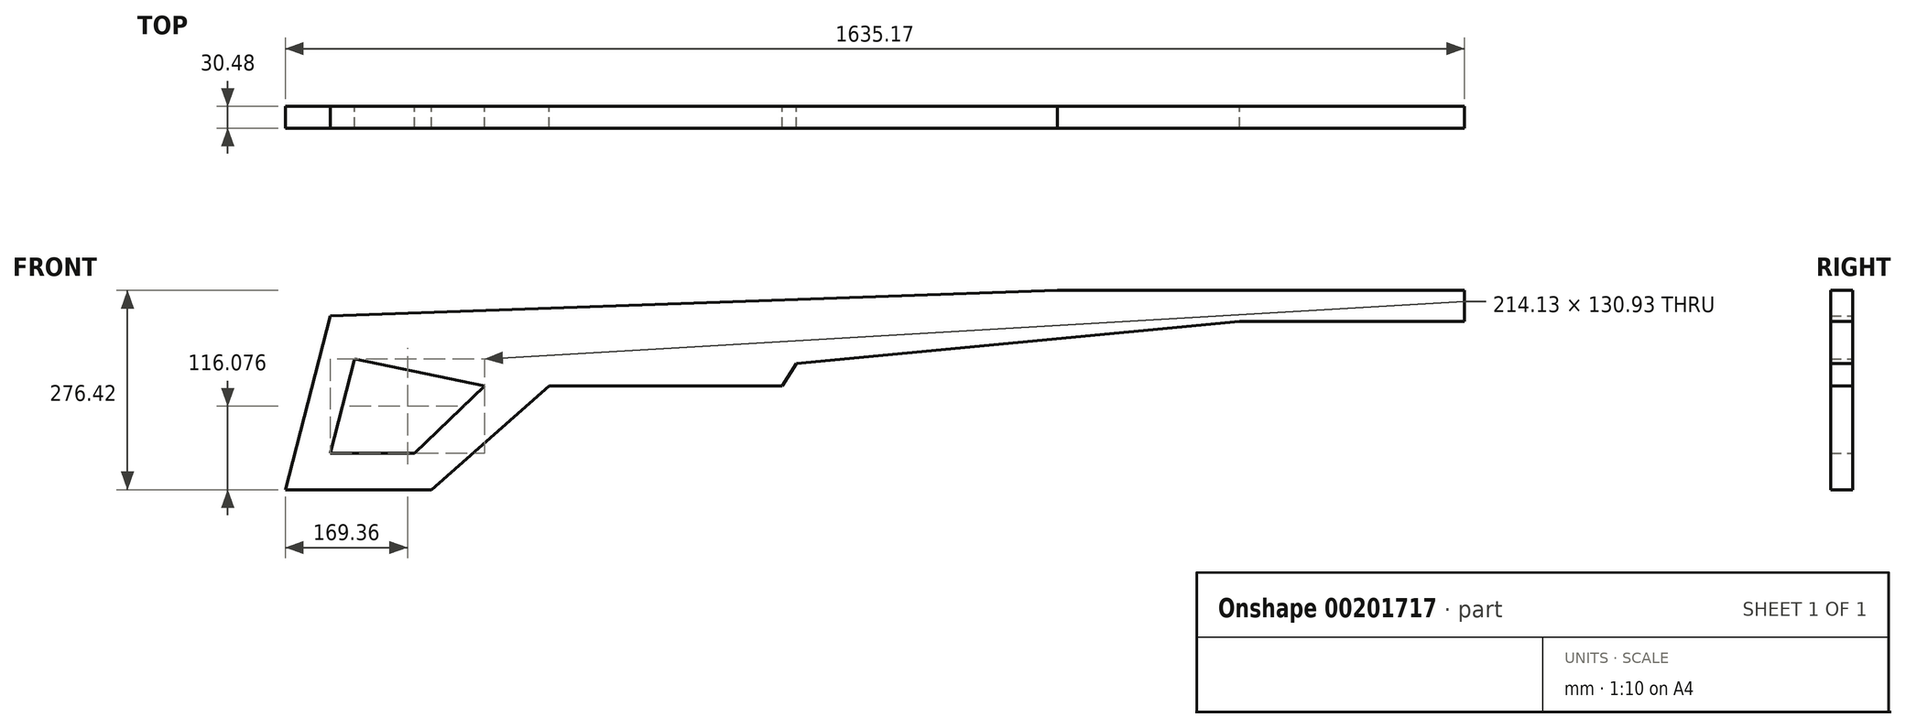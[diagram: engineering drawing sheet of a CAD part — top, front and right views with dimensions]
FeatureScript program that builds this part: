
annotation { "Feature Type Name" : "Feature", "Feature Type Description" : "" }
export const myFeature = defineFeature(function(context is Context, id is Id, definition is map)
    precondition{}
    {
        {
            var Q0;
            Q0=qCreatedBy(makeId("Front.planeOp"),FACE);
            var sketch = newSketch(context, id + "F0", { "sketchPlane" : qUnion([Q0])});
            skLineSegment(sketch, "E0", {"start": v(-1066.38, 97.68) * mm, "end": v(-58.03, 132.72) * mm});
            skLineSegment(sketch, "E1", {"start": v(-1066.38, 97.68) * mm, "end": v(-1128.68, -143.7) * mm});
            skLineSegment(sketch, "E2", {"start": v(-1128.68, -143.7) * mm, "end": v(-926.23, -143.7) * mm});
            skLineSegment(sketch, "E3", {"start": v(-926.23, -143.7) * mm, "end": v(-762.71, 0) * mm});
            skLineSegment(sketch, "E4", {"start": v(-762.71, 0) * mm, "end": v(-439.57, 0) * mm});
            skLineSegment(sketch, "E5", {"start": v(-420.1, 31.5) * mm, "end": v(195.03, 89.9) * mm});
            skLineSegment(sketch, "E6", {"start": v(-439.57, 0) * mm, "end": v(-420.1, 31.5) * mm});
            skLineSegment(sketch, "E7", {"start": v(-58.03, 132.72) * mm, "end": v(506.49, 132.72) * mm});
            skLineSegment(sketch, "E8", {"start": v(195.03, 89.9) * mm, "end": v(506.49, 89.9) * mm});
            skLineSegment(sketch, "E9", {"start": v(506.49, 132.72) * mm, "end": v(506.49, 89.9) * mm});
            skLineSegment(sketch, "E10", {"start": v(-1066.38, -93.1) * mm, "end": v(-1032.6, 37.84) * mm});
            skLineSegment(sketch, "E11", {"start": v(-1066.38, -93.1) * mm, "end": v(-949.59, -93.1) * mm});
            skLineSegment(sketch, "E12", {"start": v(-852.26, 0) * mm, "end": v(-949.59, -93.1) * mm});
            skLineSegment(sketch, "E13", {"start": v(-1032.6, 37.84) * mm, "end": v(-852.26, 0) * mm});
            skSolve(sketch);
        }
        {
            var Q0;
            Q0=makeQuery(id+"F0.imprint","IMPRINT",FACE,{"disambiguationData":[TD([[makeQuery(id+"F0.imprint","IMPRINT",EDGE,{"derivedFrom":sQuery(id+"F0.wireOp",EDGE,"E0")}),-1.0]])]});
            extrude(context, id + "F1", {"entities" : qUnion([Q0]), "depth" : 30.48 * mm});
        }
    });
